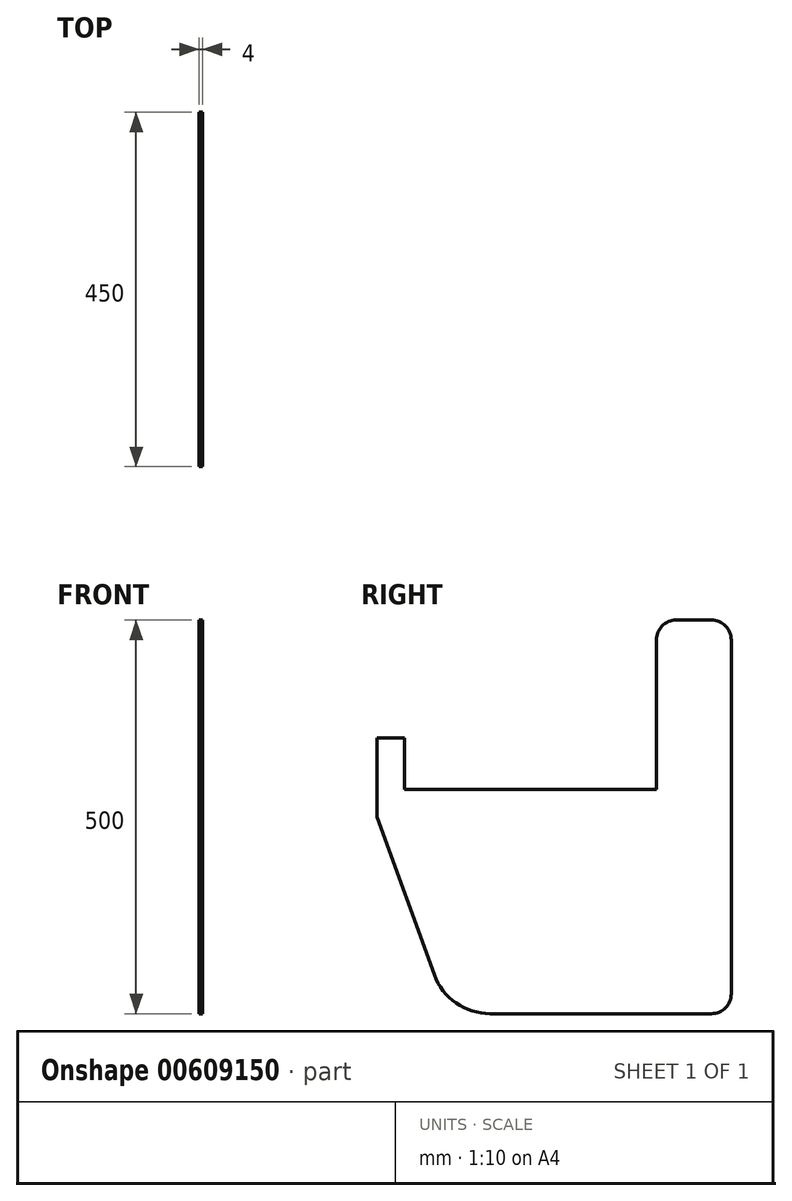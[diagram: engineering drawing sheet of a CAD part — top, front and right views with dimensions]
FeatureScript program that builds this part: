
annotation { "Feature Type Name" : "Feature", "Feature Type Description" : "" }
export const myFeature = defineFeature(function(context is Context, id is Id, definition is map)
    precondition{}
    {
        {
            var Q0;
            Q0=qCreatedBy(makeId("Right.planeOp"),FACE);
            var sketch = newSketch(context, id + "F0", { "sketchPlane" : qUnion([Q0])});
            skLineSegment(sketch, "E0", {"start": v(0, 0) * mm, "end": v(73.03, -200.65) * mm});
            skLineSegment(sketch, "E1", {"start": v(143.5, -250) * mm, "end": v(425, -250) * mm});
            skLineSegment(sketch, "E2", {"start": v(450, -225) * mm, "end": v(450, 0) * mm});
            skArc(sketch, "E3", {"start": v(73.03, -200.65) * mm, "mid": v(100.49, -236.44) * mm, "end": v(143.5, -250) * mm});
            skLineSegment(sketch, "E4", {"start": v(0, 0) * mm, "end": v(450, 0) * mm, "construction": true});
            skPoint(sketch, "E5.visualSharp", {"position": v(450, -250) * mm});
            skArc(sketch, "E5.filletArc", {"start": v(425, -250) * mm, "mid": v(442.68, -242.68) * mm, "end": v(450, -225) * mm});
            skLineSegment(sketch, "E6", {"start": v(450, 0) * mm, "end": v(450, 225) * mm});
            skLineSegment(sketch, "E7", {"start": v(425, 250) * mm, "end": v(380, 250) * mm});
            skLineSegment(sketch, "E8", {"start": v(355, 225) * mm, "end": v(355, 35) * mm});
            skLineSegment(sketch, "E9", {"start": v(355, 35) * mm, "end": v(35, 35) * mm});
            skLineSegment(sketch, "E10", {"start": v(35, 35) * mm, "end": v(35, 100) * mm});
            skLineSegment(sketch, "E11", {"start": v(35, 100) * mm, "end": v(0, 100) * mm});
            skLineSegment(sketch, "E12", {"start": v(0, 100) * mm, "end": v(0, 0) * mm});
            skPoint(sketch, "E13.visualSharp", {"position": v(355, 250) * mm});
            skArc(sketch, "E13.filletArc", {"start": v(380, 250) * mm, "mid": v(362.32, 242.68) * mm, "end": v(355, 225) * mm});
            skPoint(sketch, "E14.visualSharp", {"position": v(450, 250) * mm});
            skArc(sketch, "E14.filletArc", {"start": v(450, 225) * mm, "mid": v(442.68, 242.68) * mm, "end": v(425, 250) * mm});
            skSolve(sketch);
        }
        {
            var Q0;
            Q0 = qSketchRegion(id + "F0", true);
            extrude(context, id + "F1", {"entities" : qUnion([Q0]), "depth" : 2 * mm, "offsetDistance" : 25 * mm, "hasSecondDirection" : true, "secondDirectionOppositeDirection" : true, "secondDirectionDepth" : 2 * mm});
        }
    });
